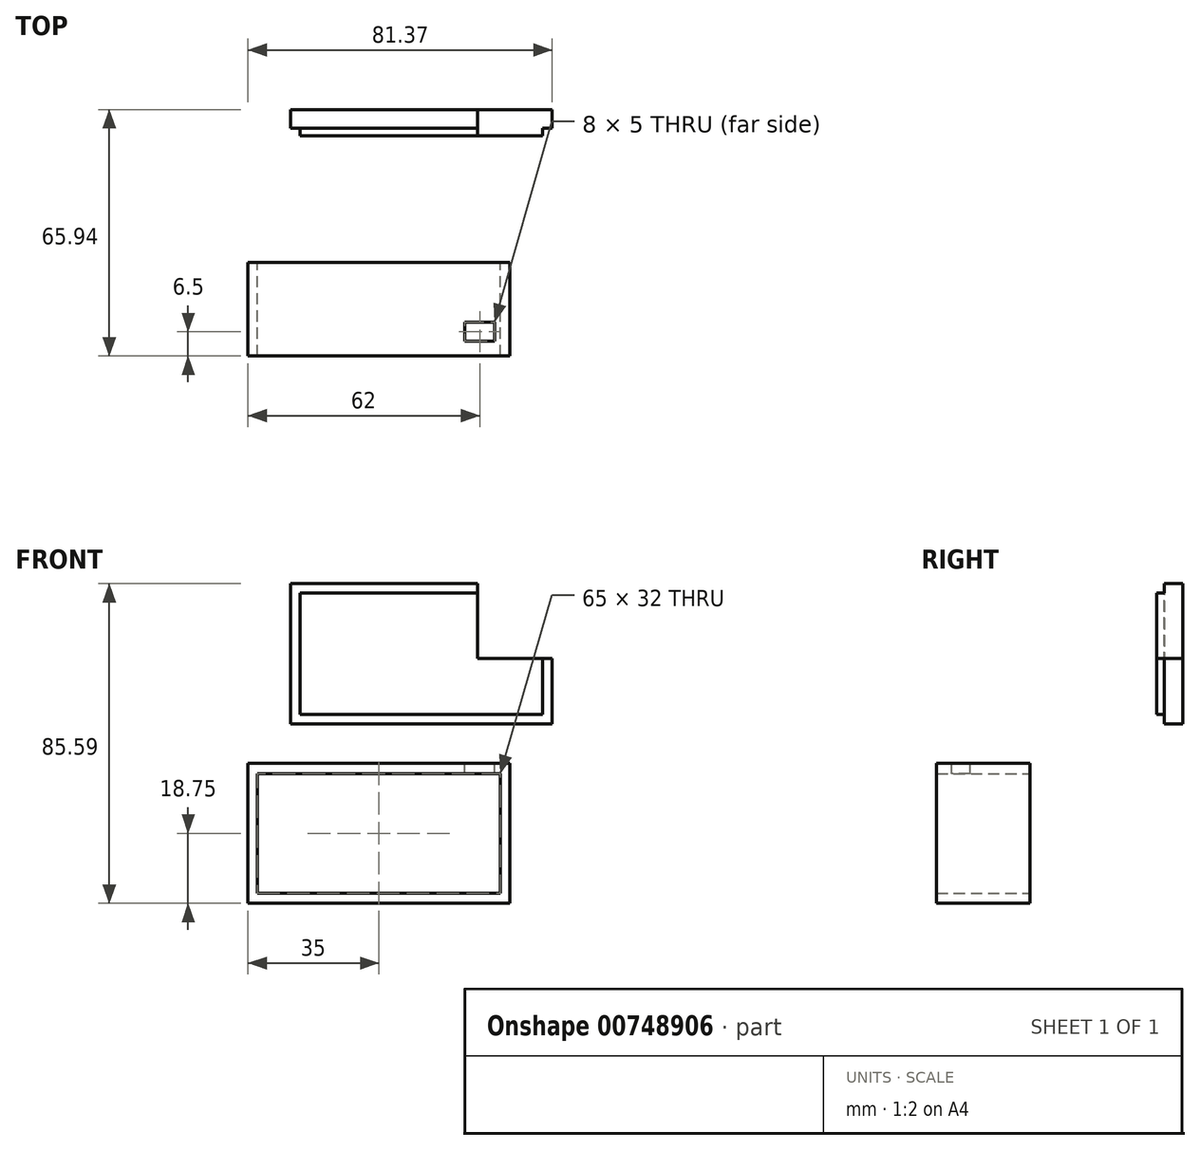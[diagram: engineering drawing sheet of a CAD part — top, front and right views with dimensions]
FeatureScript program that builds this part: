
annotation { "Feature Type Name" : "Feature", "Feature Type Description" : "" }
export const myFeature = defineFeature(function(context is Context, id is Id, definition is map)
    precondition{}
    {
        {
            var Q0;
            Q0=qCreatedBy(makeId("Front.planeOp"),FACE);
            var sketch = newSketch(context, id + "F0", { "sketchPlane" : qUnion([Q0])});
            skLineSegment(sketch, "E0.bottom", {"start": v(-32.5, 16) * mm, "end": v(32.5, 16) * mm});
            skLineSegment(sketch, "E0.top", {"start": v(-32.5, -16) * mm, "end": v(32.5, -16) * mm});
            skLineSegment(sketch, "E0.left", {"start": v(-32.5, 16) * mm, "end": v(-32.5, -16) * mm});
            skLineSegment(sketch, "E0.right", {"start": v(32.5, 16) * mm, "end": v(32.5, -16) * mm});
            skLineSegment(sketch, "E1.bottom", {"start": v(35, -18.75) * mm, "end": v(-35, -18.75) * mm});
            skLineSegment(sketch, "E1.top", {"start": v(35, 18.75) * mm, "end": v(-35, 18.75) * mm});
            skLineSegment(sketch, "E1.left", {"start": v(35, -18.75) * mm, "end": v(35, 18.75) * mm});
            skLineSegment(sketch, "E1.right", {"start": v(-35, -18.75) * mm, "end": v(-35, 18.75) * mm});
            skPoint(sketch, "E1.middle", {"position": v(0, 0) * mm});
            skSolve(sketch);
        }
        {
            var Q0;
            Q0=makeQuery(id+"F0.imprint","IMPRINT",FACE,{"disambiguationData":[TD([[makeQuery(id+"F0.imprint","IMPRINT",EDGE,{"derivedFrom":sQuery(id+"F0.wireOp",EDGE,"E0.bottom")}),1.0]])]});
            extrude(context, id + "F1", {"entities" : qUnion([Q0]), "depth" : 25 * mm, "offsetDistance" : 25 * mm});
        }
        {
            var Q0;
            Q0=qCreatedBy(makeId("Front.planeOp"),FACE);
            var sketch = newSketch(context, id + "F2", { "sketchPlane" : qUnion([Q0])});
            skLineSegment(sketch, "E2.bottom", {"start": v(-23.63, 66.84) * mm, "end": v(46.37, 66.84) * mm});
            skLineSegment(sketch, "E2.top", {"start": v(-23.63, 29.34) * mm, "end": v(46.37, 29.34) * mm});
            skLineSegment(sketch, "E2.left", {"start": v(-23.63, 66.84) * mm, "end": v(-23.63, 29.34) * mm});
            skLineSegment(sketch, "E2.right", {"start": v(46.37, 66.84) * mm, "end": v(46.37, 29.34) * mm});
            skSolve(sketch);
        }
        {
            var Q0;
            Q0 = qSketchRegion(id + "F2", true);
            extrude(context, id + "F3", {"entities" : qUnion([Q0]), "depth" : 5 * mm, "offsetDistance" : 25 * mm});
        }
        {
            var Q0;
            Q0=makeQuery(id+"F3.opExtrude","CAP_FACE",FACE,{"disambiguationData":[OSD([sQuery(id+"F2.wireOp",EDGE,"E2.bottom"),sQuery(id+"F2.wireOp",EDGE,"E2.top"),sQuery(id+"F2.wireOp",EDGE,"E2.left"),sQuery(id+"F2.wireOp",EDGE,"E2.right")])],"isStart":false});
            var sketch = newSketch(context, id + "F4", { "sketchPlane" : qUnion([Q0])});
            skLineSegment(sketch, "E3.bottom", {"start": v(43.87, 31.84) * mm, "end": v(-21.13, 31.84) * mm});
            skLineSegment(sketch, "E3.top", {"start": v(43.87, 64.34) * mm, "end": v(-21.13, 64.34) * mm});
            skLineSegment(sketch, "E3.left", {"start": v(43.87, 31.84) * mm, "end": v(43.87, 64.34) * mm});
            skLineSegment(sketch, "E3.right", {"start": v(-21.13, 31.84) * mm, "end": v(-21.13, 64.34) * mm});
            skPoint(sketch, "E3.middle", {"position": v(11.37, 48.09) * mm});
            skPoint(sketch, "E3.middle.positionSnap0", {"position": v(11.37, 66.84) * mm});
            skPoint(sketch, "E3.centerSnap0", {"position": v(11.37, 66.84) * mm});
            skSolve(sketch);
        }
        {
            var Q0;
            Q0 = qSketchRegion(id + "F4", true);
            extrude(context, id + "F5", {"entities" : qUnion([Q0]), "operationType" : NewBodyOperationType.ADD, "depth" : 2 * mm, "offsetDistance" : 25 * mm});
        }
        {
            var Q0;
            Q0=makeQuery(id+"F3.opExtrude","CAP_FACE",FACE,{"disambiguationData":[OSD([sQuery(id+"F2.wireOp",EDGE,"E2.bottom"),sQuery(id+"F2.wireOp",EDGE,"E2.top"),sQuery(id+"F2.wireOp",EDGE,"E2.left"),sQuery(id+"F2.wireOp",EDGE,"E2.right")])],"isStart":true});
            var sketch = newSketch(context, id + "F6", { "sketchPlane" : qUnion([Q0])});
            skLineSegment(sketch, "E4.bottom", {"start": v(-46.37, 66.84) * mm, "end": v(-26.37, 66.84) * mm});
            skLineSegment(sketch, "E4.top", {"start": v(-46.37, 46.84) * mm, "end": v(-26.37, 46.84) * mm});
            skLineSegment(sketch, "E4.left", {"start": v(-46.37, 66.84) * mm, "end": v(-46.37, 46.84) * mm});
            skLineSegment(sketch, "E4.right", {"start": v(-26.37, 66.84) * mm, "end": v(-26.37, 46.84) * mm});
            skSolve(sketch);
        }
        {
            var Q0;
            Q0 = qSketchRegion(id + "F6", true);
            extrude(context, id + "F7", {"entities" : qUnion([Q0]), "operationType" : NewBodyOperationType.REMOVE, "oppositeDirection" : true, "depth" : 25 * mm, "offsetDistance" : 25 * mm});
        }
        {
            var Q0;
            Q0=makeQuery(id+"F3.opExtrude","SWEPT_BODY",BODY,{"disambiguationData":[OSD([sQuery(id+"F2.wireOp",EDGE,"E2.bottom"),sQuery(id+"F2.wireOp",EDGE,"E2.top"),sQuery(id+"F2.wireOp",EDGE,"E2.left"),sQuery(id+"F2.wireOp",EDGE,"E2.right")])]});
            transform(context, id + "F8", {"entities" : qUnion([Q0]), "transformType" : TransformType.TRANSLATION_3D, "dx" : 0 * mm, "dy" : 40.94 * mm, "dz" : 0 * mm, "makeCopy" : false});
        }
        {
            var Q0;
            Q0=makeQuery(id+"F1.opExtrude","SWEPT_FACE",FACE,{"disambiguationData":[OSD([sQuery(id+"F0.wireOp",EDGE,"E1.top")])]});
            var sketch = newSketch(context, id + "F9", { "sketchPlane" : qUnion([Q0])});
            skLineSegment(sketch, "E5.bottom", {"start": v(23, -16) * mm, "end": v(31, -16) * mm});
            skLineSegment(sketch, "E5.top", {"start": v(23, -21) * mm, "end": v(31, -21) * mm});
            skLineSegment(sketch, "E5.left", {"start": v(23, -16) * mm, "end": v(23, -21) * mm});
            skLineSegment(sketch, "E5.right", {"start": v(31, -16) * mm, "end": v(31, -21) * mm});
            skSolve(sketch);
        }
        {
            var Q0;
            Q0 = qSketchRegion(id + "F9", true);
            extrude(context, id + "F10", {"entities" : qUnion([Q0]), "operationType" : NewBodyOperationType.REMOVE, "oppositeDirection" : true, "depth" : 25 * mm, "offsetDistance" : 25 * mm});
        }
    });
